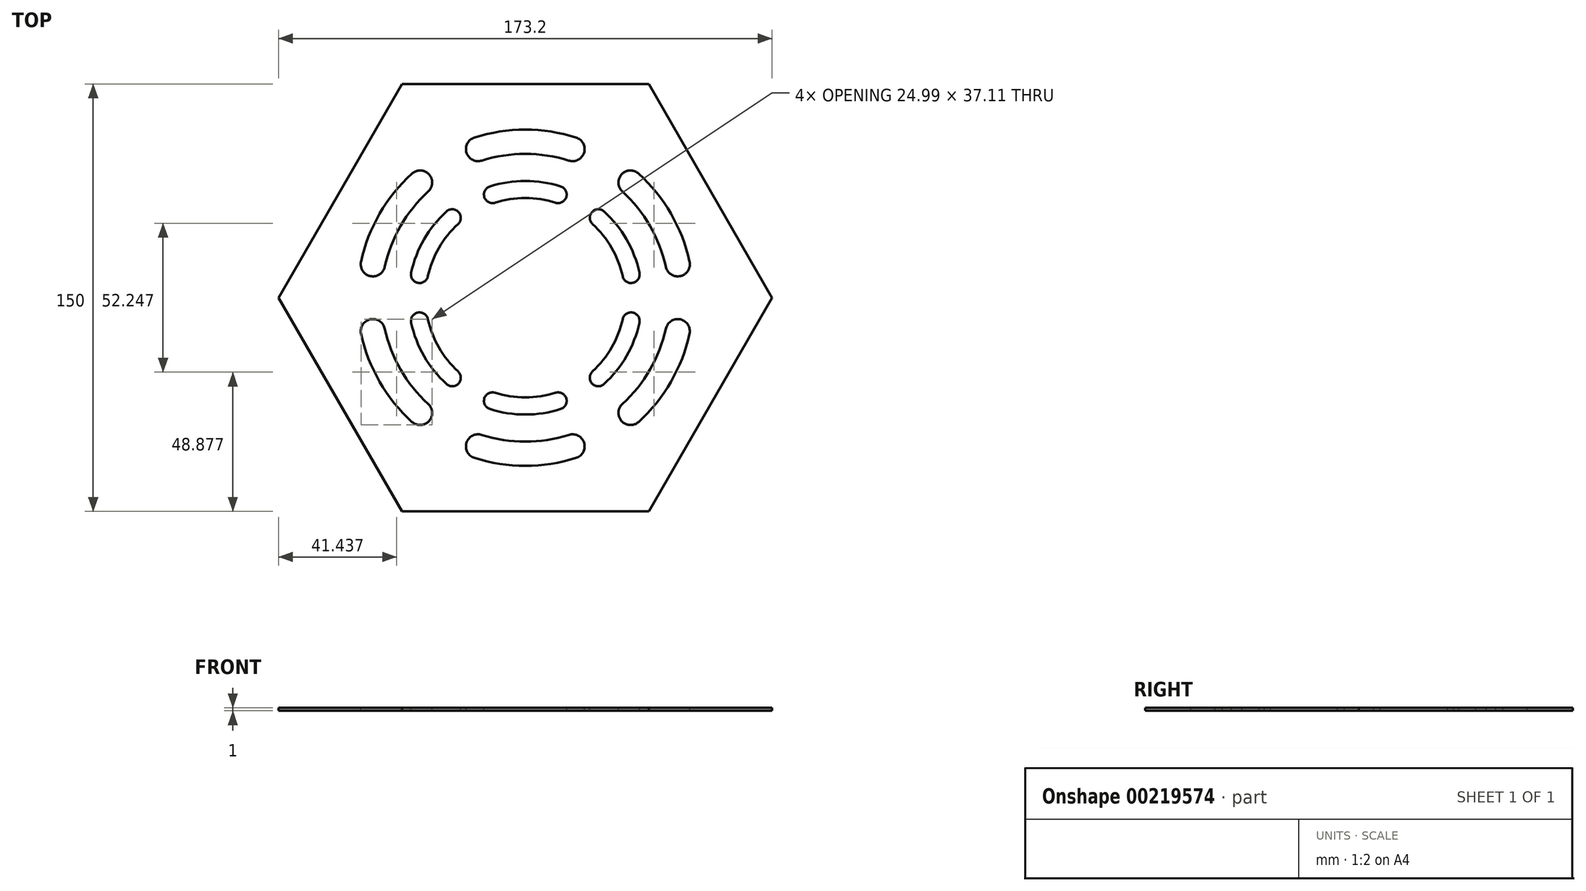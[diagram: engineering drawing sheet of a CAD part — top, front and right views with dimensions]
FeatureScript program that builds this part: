
annotation { "Feature Type Name" : "Feature", "Feature Type Description" : "" }
export const myFeature = defineFeature(function(context is Context, id is Id, definition is map)
    precondition{}
    {
        {
            var Q0;
            Q0=qCreatedBy(makeId("Top.planeOp"),FACE);
            var sketch = newSketch(context, id + "F0", { "sketchPlane" : qUnion([Q0])});
            skCircle(sketch, "E0.cCircle", {"center": v(0, 0) * mm, "radius": 75 * mm, "construction": true});
            skLineSegment(sketch, "E0.0", {"start": v(43.3, 75) * mm, "end": v(86.6, 0) * mm});
            skLineSegment(sketch, "E0.1", {"start": v(86.6, 0) * mm, "end": v(43.3, -75) * mm});
            skLineSegment(sketch, "E0.2", {"start": v(43.3, -75) * mm, "end": v(-43.3, -75) * mm});
            skLineSegment(sketch, "E0.3", {"start": v(-43.3, -75) * mm, "end": v(-86.6, 0) * mm});
            skLineSegment(sketch, "E0.4", {"start": v(-86.6, 0) * mm, "end": v(-43.3, 75) * mm});
            skLineSegment(sketch, "E0.5", {"start": v(-43.3, 75) * mm, "end": v(43.3, 75) * mm});
            skPoint(sketch, "E0.0.midPoint", {"position": v(64.95, 37.5) * mm});
            skSolve(sketch);
        }
        {
            var Q0;
            Q0 = qSketchRegion(id + "F0", true);
            extrude(context, id + "F1", {"entities" : qUnion([Q0]), "depth" : 1 * mm});
        }
        {
            var Q0;
            Q0=makeQuery(id+"F1.opExtrude","CAP_FACE",FACE,{"disambiguationData":[OSD([sQuery(id+"F0.wireOp",EDGE,"E0.0"),sQuery(id+"F0.wireOp",EDGE,"E0.1"),sQuery(id+"F0.wireOp",EDGE,"E0.2"),sQuery(id+"F0.wireOp",EDGE,"E0.3"),sQuery(id+"F0.wireOp",EDGE,"E0.4"),sQuery(id+"F0.wireOp",EDGE,"E0.5")])],"isStart":false});
            var sketch = newSketch(context, id + "F2", { "sketchPlane" : qUnion([Q0])});
            skArc(sketch, "E1", {"start": v(57.63, 12.66) * mm, "mid": v(51.1, 29.5) * mm, "end": v(39.78, 43.57) * mm});
            skLineSegment(sketch, "E2", {"start": v(0, 0) * mm, "end": v(39.78, 43.57) * mm, "construction": true});
            skLineSegment(sketch, "E3", {"start": v(0, 0) * mm, "end": v(57.63, 12.66) * mm, "construction": true});
            skArc(sketch, "E4", {"start": v(49.32, 10.84) * mm, "mid": v(43.73, 25.25) * mm, "end": v(34.05, 37.3) * mm});
            skCircle(sketch, "E5", {"center": v(36.91, 40.44) * mm, "radius": 4.25 * mm});
            skCircle(sketch, "E6", {"center": v(53.47, 11.75) * mm, "radius": 4.25 * mm});
            skCircle(sketch, "E7.1.0", {"center": v(-16.56, 52.19) * mm, "radius": 4.25 * mm});
            skArc(sketch, "E7.1.1", {"start": v(17.85, 56.24) * mm, "mid": v(0, 59) * mm, "end": v(-17.85, 56.24) * mm});
            skArc(sketch, "E7.1.2", {"start": v(15.28, 48.13) * mm, "mid": v(0, 50.5) * mm, "end": v(-15.28, 48.13) * mm});
            skCircle(sketch, "E7.1.3", {"center": v(16.56, 52.19) * mm, "radius": 4.25 * mm});
            skCircle(sketch, "E7.2.0", {"center": v(-53.47, 11.75) * mm, "radius": 4.25 * mm});
            skArc(sketch, "E7.2.1", {"start": v(-39.78, 43.57) * mm, "mid": v(-51.1, 29.5) * mm, "end": v(-57.63, 12.66) * mm});
            skArc(sketch, "E7.2.2", {"start": v(-34.05, 37.3) * mm, "mid": v(-43.73, 25.25) * mm, "end": v(-49.32, 10.84) * mm});
            skCircle(sketch, "E7.2.3", {"center": v(-36.91, 40.44) * mm, "radius": 4.25 * mm});
            skCircle(sketch, "E7.3.0", {"center": v(-36.91, -40.44) * mm, "radius": 4.25 * mm});
            skArc(sketch, "E7.3.1", {"start": v(-57.63, -12.66) * mm, "mid": v(-51.1, -29.5) * mm, "end": v(-39.78, -43.57) * mm});
            skArc(sketch, "E7.3.2", {"start": v(-49.32, -10.84) * mm, "mid": v(-43.73, -25.25) * mm, "end": v(-34.05, -37.3) * mm});
            skCircle(sketch, "E7.3.3", {"center": v(-53.47, -11.75) * mm, "radius": 4.25 * mm});
            skCircle(sketch, "E7.4.0", {"center": v(16.56, -52.19) * mm, "radius": 4.25 * mm});
            skArc(sketch, "E7.4.1", {"start": v(-17.85, -56.24) * mm, "mid": v(0, -59) * mm, "end": v(17.85, -56.24) * mm});
            skArc(sketch, "E7.4.2", {"start": v(-15.28, -48.13) * mm, "mid": v(0, -50.5) * mm, "end": v(15.28, -48.13) * mm});
            skCircle(sketch, "E7.4.3", {"center": v(-16.56, -52.19) * mm, "radius": 4.25 * mm});
            skCircle(sketch, "E7.5.0", {"center": v(53.47, -11.75) * mm, "radius": 4.25 * mm});
            skArc(sketch, "E7.5.1", {"start": v(39.78, -43.57) * mm, "mid": v(51.1, -29.5) * mm, "end": v(57.63, -12.66) * mm});
            skArc(sketch, "E7.5.2", {"start": v(34.05, -37.3) * mm, "mid": v(43.73, -25.25) * mm, "end": v(49.32, -10.84) * mm});
            skCircle(sketch, "E7.5.3", {"center": v(36.91, -40.44) * mm, "radius": 4.25 * mm});
            skLineSegment(sketch, "E8", {"start": v(53.47, 11.75) * mm, "end": v(53.47, -11.75) * mm, "construction": true});
            skPoint(sketch, "E9", {"position": v(53.47, 7.5) * mm});
            skPoint(sketch, "E10", {"position": v(53.47, -7.5) * mm});
            skArc(sketch, "E11", {"start": v(40.04, 8.8) * mm, "mid": v(35.5, 20.5) * mm, "end": v(27.64, 30.28) * mm});
            skArc(sketch, "E12", {"start": v(34.18, 7.51) * mm, "mid": v(30.31, 17.5) * mm, "end": v(23.6, 25.85) * mm});
            skCircle(sketch, "E13", {"center": v(37.11, 8.16) * mm, "radius": 3 * mm});
            skCircle(sketch, "E14", {"center": v(25.62, 28.06) * mm, "radius": 3 * mm});
            skCircle(sketch, "E15.1.0", {"center": v(-11.5, 36.22) * mm, "radius": 3 * mm});
            skArc(sketch, "E15.1.1", {"start": v(12.4, 39.08) * mm, "mid": v(0, 41) * mm, "end": v(-12.4, 39.08) * mm});
            skCircle(sketch, "E15.1.2", {"center": v(11.5, 36.22) * mm, "radius": 3 * mm});
            skArc(sketch, "E15.1.3", {"start": v(10.59, 33.36) * mm, "mid": v(0, 35) * mm, "end": v(-10.59, 33.36) * mm});
            skCircle(sketch, "E15.2.0", {"center": v(-37.11, 8.16) * mm, "radius": 3 * mm});
            skArc(sketch, "E15.2.1", {"start": v(-27.64, 30.28) * mm, "mid": v(-35.5, 20.5) * mm, "end": v(-40.04, 8.8) * mm});
            skCircle(sketch, "E15.2.2", {"center": v(-25.62, 28.06) * mm, "radius": 3 * mm});
            skArc(sketch, "E15.2.3", {"start": v(-23.6, 25.85) * mm, "mid": v(-30.31, 17.5) * mm, "end": v(-34.18, 7.51) * mm});
            skCircle(sketch, "E15.3.0", {"center": v(-25.62, -28.06) * mm, "radius": 3 * mm});
            skArc(sketch, "E15.3.1", {"start": v(-40.04, -8.8) * mm, "mid": v(-35.5, -20.5) * mm, "end": v(-27.64, -30.28) * mm});
            skCircle(sketch, "E15.3.2", {"center": v(-37.11, -8.16) * mm, "radius": 3 * mm});
            skArc(sketch, "E15.3.3", {"start": v(-34.18, -7.51) * mm, "mid": v(-30.31, -17.5) * mm, "end": v(-23.6, -25.85) * mm});
            skCircle(sketch, "E15.4.0", {"center": v(11.5, -36.22) * mm, "radius": 3 * mm});
            skArc(sketch, "E15.4.1", {"start": v(-12.4, -39.08) * mm, "mid": v(0, -41) * mm, "end": v(12.4, -39.08) * mm});
            skCircle(sketch, "E15.4.2", {"center": v(-11.5, -36.22) * mm, "radius": 3 * mm});
            skArc(sketch, "E15.4.3", {"start": v(-10.59, -33.36) * mm, "mid": v(0, -35) * mm, "end": v(10.59, -33.36) * mm});
            skCircle(sketch, "E15.5.0", {"center": v(37.11, -8.16) * mm, "radius": 3 * mm});
            skArc(sketch, "E15.5.1", {"start": v(27.64, -30.28) * mm, "mid": v(35.5, -20.5) * mm, "end": v(40.04, -8.8) * mm});
            skCircle(sketch, "E15.5.2", {"center": v(25.62, -28.06) * mm, "radius": 3 * mm});
            skArc(sketch, "E15.5.3", {"start": v(23.6, -25.85) * mm, "mid": v(30.31, -17.5) * mm, "end": v(34.18, -7.51) * mm});
            skSolve(sketch);
        }
        {
            var Q0;
            Q0 = qSketchRegion(id + "F2", true);
            extrude(context, id + "F3", {"entities" : qUnion([Q0]), "operationType" : NewBodyOperationType.REMOVE, "endBound" : BoundingType.THROUGH_ALL, "oppositeDirection" : true, "depth" : 25 * mm});
        }
    });
